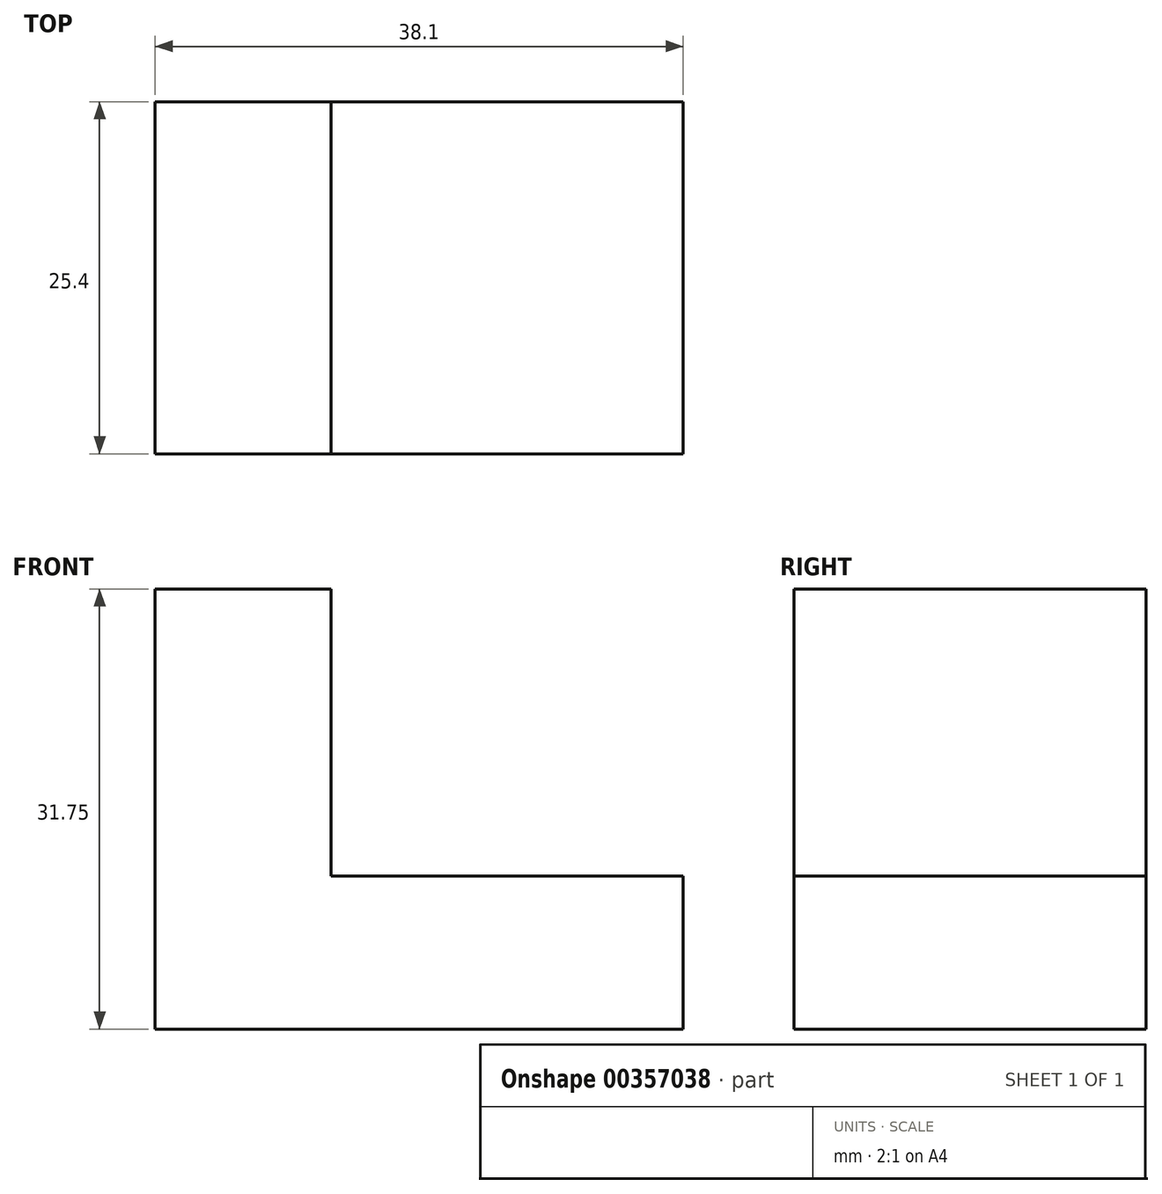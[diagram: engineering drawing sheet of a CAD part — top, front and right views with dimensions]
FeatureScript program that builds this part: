
annotation { "Feature Type Name" : "Feature", "Feature Type Description" : "" }
export const myFeature = defineFeature(function(context is Context, id is Id, definition is map)
    precondition{}
    {
        {
            var Q0;
            Q0=qCreatedBy(makeId("Front.planeOp"),FACE);
            var sketch = newSketch(context, id + "F0", { "sketchPlane" : qUnion([Q0])});
            skLineSegment(sketch, "E0", {"start": v(0, 31.75) * mm, "end": v(12.7, 31.75) * mm});
            skLineSegment(sketch, "E1", {"start": v(12.7, 31.75) * mm, "end": v(12.7, 11.04) * mm});
            skLineSegment(sketch, "E2", {"start": v(12.7, 11.04) * mm, "end": v(38.1, 11.04) * mm});
            skLineSegment(sketch, "E3", {"start": v(38.1, 11.04) * mm, "end": v(38.1, 0) * mm});
            skLineSegment(sketch, "E4", {"start": v(38.1, 0) * mm, "end": v(0, 0) * mm});
            skLineSegment(sketch, "E5", {"start": v(0, 0) * mm, "end": v(0, 31.75) * mm});
            skSolve(sketch);
        }
        {
            var Q0;
            Q0 = qSketchRegion(id + "F0", true);
            extrude(context, id + "F1", {"entities" : qUnion([Q0]), "depth" : 25.4 * mm});
        }
    });
